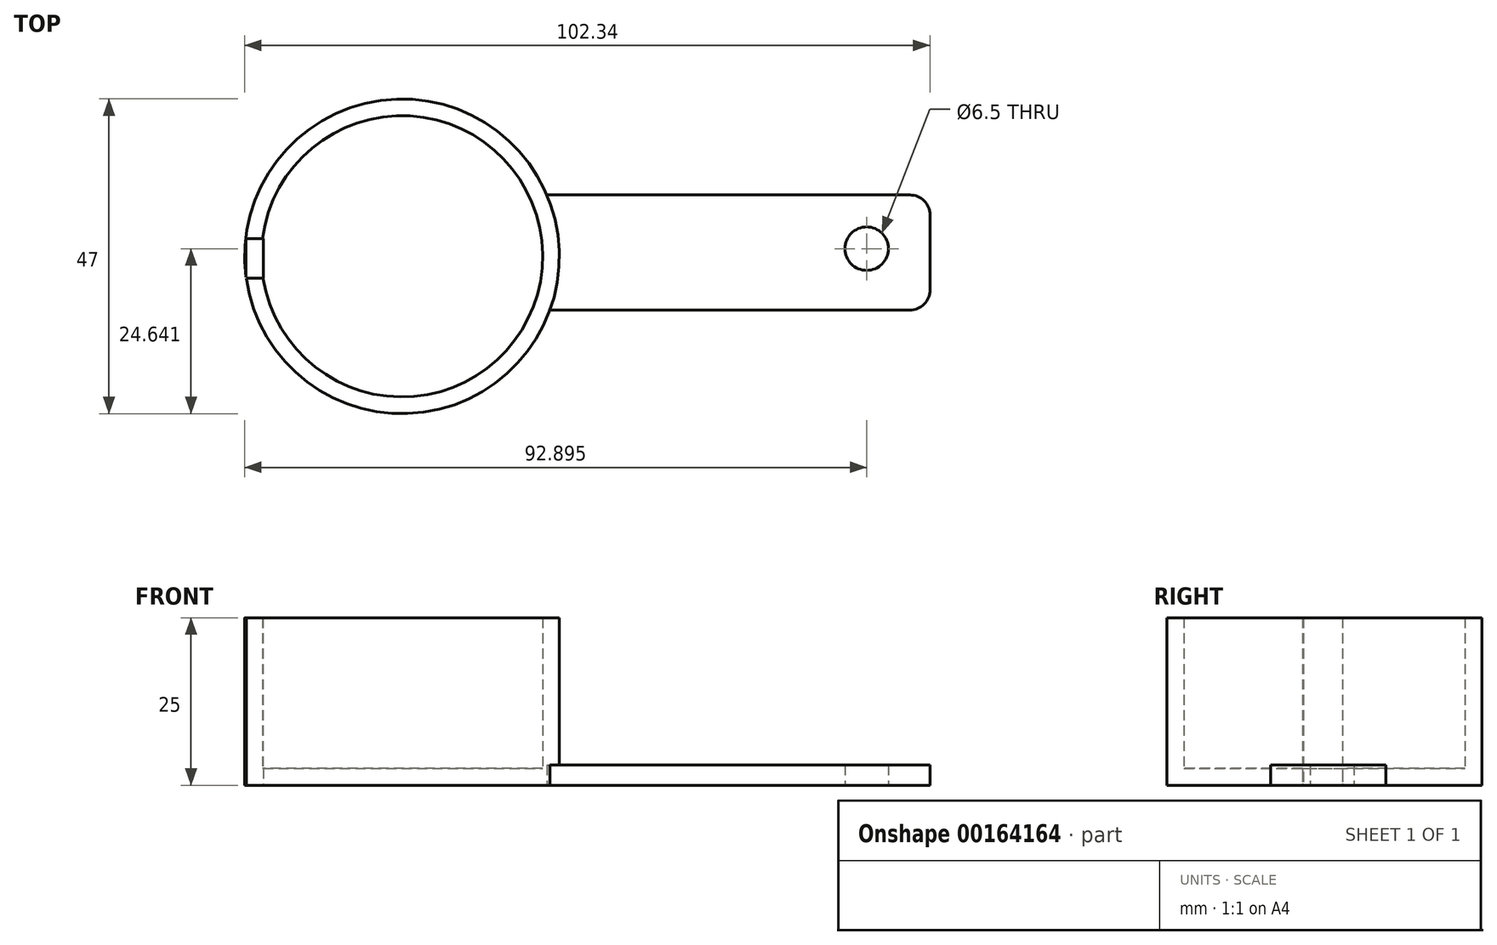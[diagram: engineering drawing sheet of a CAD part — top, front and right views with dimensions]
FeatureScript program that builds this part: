
annotation { "Feature Type Name" : "Feature", "Feature Type Description" : "" }
export const myFeature = defineFeature(function(context is Context, id is Id, definition is map)
    precondition{}
    {
        {
            var Q0;
            Q0=qCreatedBy(makeId("Top.planeOp"),FACE);
            var sketch = newSketch(context, id + "F0", { "sketchPlane" : qUnion([Q0])});
            skCircle(sketch, "E0", {"center": v(-44.3, 40) * mm, "radius": 23.5 * mm});
            skLineSegment(sketch, "E1.bottom", {"start": v(-21.88, 47.08) * mm, "end": v(30.16, 47.08) * mm});
            skLineSegment(sketch, "E1.top", {"start": v(-21.88, 32.17) * mm, "end": v(30.16, 32.17) * mm});
            skLineSegment(sketch, "E1.left", {"start": v(-21.88, 32.9) * mm, "end": v(-21.88, 32.17) * mm});
            skLineSegment(sketch, "E1.right", {"start": v(30.16, 47.08) * mm, "end": v(30.16, 32.17) * mm});
            skCircle(sketch, "E2", {"center": v(25, 40) * mm, "radius": 2.97 * mm});
            skSolve(sketch);
        }
        {
            var Q0;
            Q0=makeQuery(id+"F0.imprint","IMPRINT",FACE,{"disambiguationData":[TD([[makeQuery(id+"F0.imprint","IMPRINT",EDGE,{"derivedFrom":sQuery(id+"F0.wireOp",EDGE,"E0")}),1.0]])]});
            extrude(context, id + "F1", {"entities" : qUnion([Q0]), "depth" : 25 * mm});
        }
        {
            var Q0;
            Q0=makeQuery(id+"F1.opExtrude","CAP_FACE",FACE,{"disambiguationData":[OSD([sQuery(id+"F0.wireOp",EDGE,"E0")])],"isStart":false});
            shell(context, id + "F2", {"entities" : qUnion([Q0]), "thickness" : 2.5 * mm});
        }
        {
            var Q0;
            Q0=qCreatedBy(makeId("Top.planeOp"),FACE);
            var sketch = newSketch(context, id + "F3", { "sketchPlane" : qUnion([Q0])});
            skLineSegment(sketch, "E3.bottom", {"start": v(-23, 49.16) * mm, "end": v(34.55, 49.16) * mm});
            skLineSegment(sketch, "E3.top", {"start": v(-23, 31.98) * mm, "end": v(34.55, 31.98) * mm});
            skLineSegment(sketch, "E3.right", {"start": v(34.55, 49.16) * mm, "end": v(34.55, 31.98) * mm});
            skLineSegment(sketch, "E4.bottom", {"start": v(-67.58, 42.67) * mm, "end": v(-65, 42.67) * mm});
            skLineSegment(sketch, "E4.top", {"start": v(-67.58, 36.75) * mm, "end": v(-65, 36.75) * mm});
            skLineSegment(sketch, "E4.left", {"start": v(-67.58, 42.67) * mm, "end": v(-67.58, 36.75) * mm});
            skLineSegment(sketch, "E4.right", {"start": v(-65, 42.67) * mm, "end": v(-65, 36.75) * mm});
            skLineSegment(sketch, "E5", {"start": v(-23, 49.16) * mm, "end": v(-23, 31.98) * mm});
            skSolve(sketch);
        }
        {
            var Q0;
            Q0=makeQuery(id+"F3.imprint","IMPRINT",FACE,{"disambiguationData":[TD([[makeQuery(id+"F3.imprint","IMPRINT",EDGE,{"derivedFrom":sQuery(id+"F3.wireOp",EDGE,"E3.bottom")}),-1.0]])]});
            extrude(context, id + "F4", {"entities" : qUnion([Q0]), "operationType" : NewBodyOperationType.ADD, "depth" : 3 * mm});
        }
        {
            var Q0;
            Q0=qCreatedBy(makeId("Top.planeOp"),FACE);
            var sketch = newSketch(context, id + "F5", { "sketchPlane" : qUnion([Q0])});
            skCircle(sketch, "E6", {"center": v(25.1, 41.14) * mm, "radius": 3.5 * mm});
            skSolve(sketch);
        }
        {
            var Q0;
            Q0=sQuery(id+"F5.wireOp",VERTEX,"E6.center");
            var Q1;
            Q1=makeQuery(id+"F1.opExtrude","SWEPT_BODY",BODY,{"disambiguationData":[OSD([sQuery(id+"F0.wireOp",EDGE,"E0")])]});
            hole(context, id + "F6", {"style" : HoleStyle.SIMPLE, "endStyle" : HoleEndStyle.BLIND, "oppositeDirection" : true, "holeDiameter" : 6.5 * mm, "holeDepth" : 20 * mm, "locations" : qUnion([Q0]), "scope" : qUnion([Q1])});
        }
        {
            var Q0;
            Q0=makeQuery(id+"F3.imprint","IMPRINT",FACE,{"disambiguationData":[TD([[makeQuery(id+"F3.imprint","IMPRINT",EDGE,{"derivedFrom":sQuery(id+"F3.wireOp",EDGE,"E4.bottom")}),-1.0]])]});
            extrude(context, id + "F7", {"entities" : qUnion([Q0]), "operationType" : NewBodyOperationType.REMOVE, "depth" : 25 * mm});
        }
        {
            var Q0;
            Q0=makeQuery(id+"F4.opExtrude","SWEPT_EDGE",EDGE,{"disambiguationData":[OSD([sQuery(id+"F3.wireOp",EDGE,"E3.top"),sQuery(id+"F3.wireOp",EDGE,"E3.right")])]});
            var Q1;
            Q1=makeQuery(id+"F4.opExtrude","SWEPT_EDGE",EDGE,{"disambiguationData":[OSD([sQuery(id+"F3.wireOp",EDGE,"E3.bottom"),sQuery(id+"F3.wireOp",EDGE,"E3.right")])]});
            fillet(context, id + "F8", {"entities" : qUnion([Q0, Q1]), "radius" : 3 * mm, "tangentPropagation" : true, "allowEdgeOverflow" : false});
        }
    });
